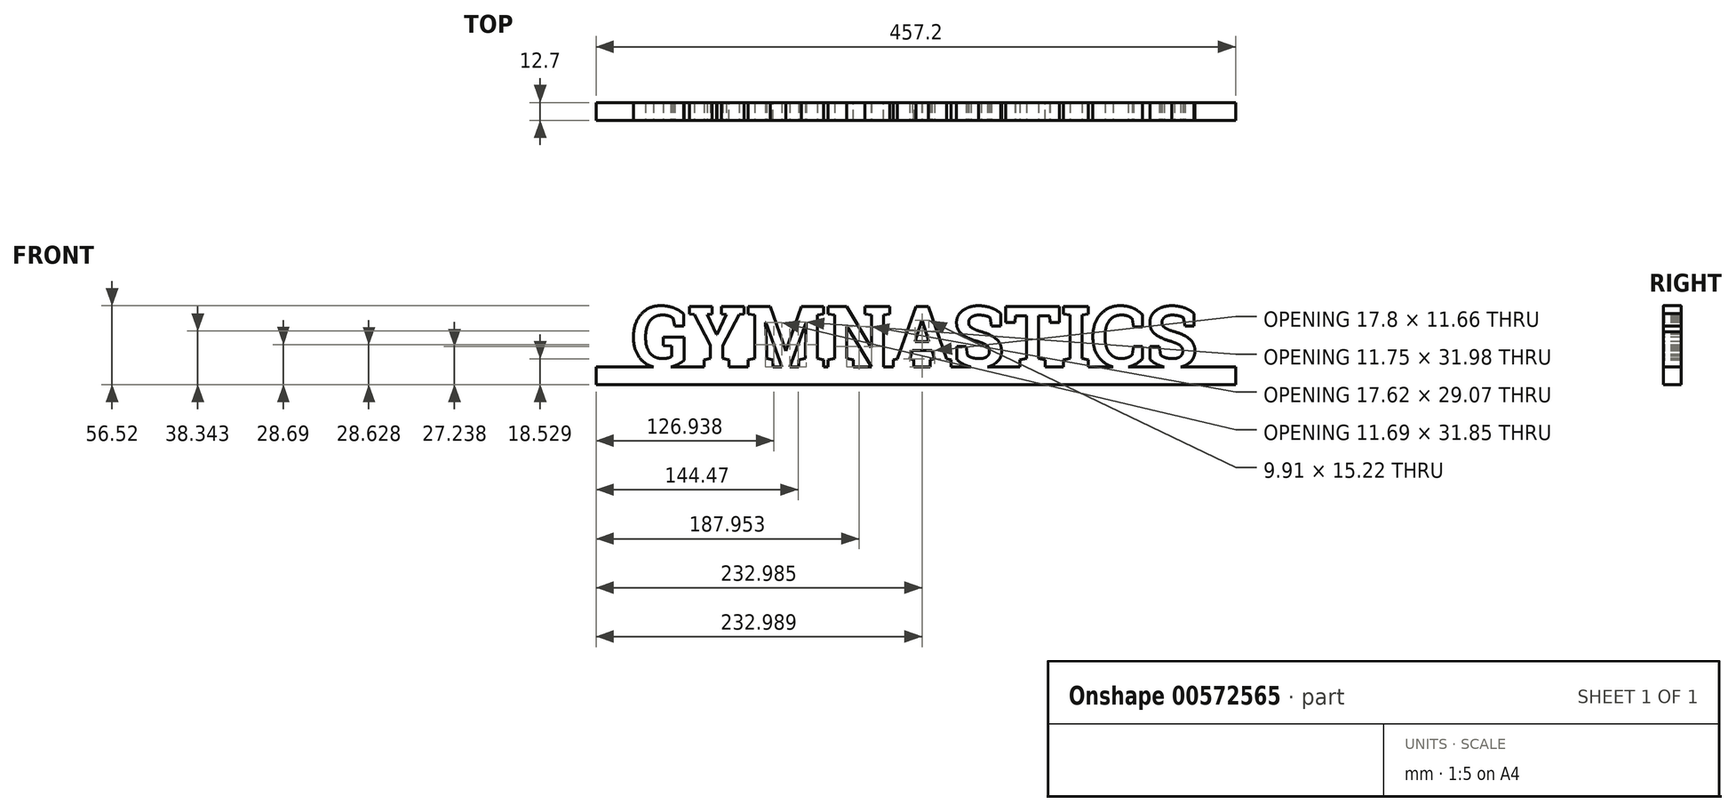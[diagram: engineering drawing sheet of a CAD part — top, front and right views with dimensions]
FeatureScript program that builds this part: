
annotation { "Feature Type Name" : "Feature", "Feature Type Description" : "" }
export const myFeature = defineFeature(function(context is Context, id is Id, definition is map)
    precondition{}
    {
        {
            var Q0;
            Q0=qCreatedBy(makeId("Front.planeOp"),FACE);
            var sketch = newSketch(context, id + "F0", { "sketchPlane" : qUnion([Q0])});
            skLineSegment(sketch, "E0.bottom", {"start": v(-211.92, -89.49) * mm, "end": v(245.28, -89.49) * mm});
            skLineSegment(sketch, "E0.top", {"start": v(-211.92, -102.19) * mm, "end": v(245.28, -102.19) * mm});
            skLineSegment(sketch, "E0.left", {"start": v(-211.92, -89.49) * mm, "end": v(-211.92, -102.19) * mm});
            skLineSegment(sketch, "E0.right", {"start": v(245.28, -89.49) * mm, "end": v(245.28, -102.19) * mm});
            skSolve(sketch);
        }
        {
            var Q0;
            Q0=makeQuery(id+"F0.imprint","IMPRINT",FACE,{"disambiguationData":[TD([[makeQuery(id+"F0.imprint","IMPRINT",EDGE,{"derivedFrom":sQuery(id+"F0.wireOp",EDGE,"E0.bottom")}),-1.0]])]});
            extrude(context, id + "F1", {"entities" : qUnion([Q0]), "depth" : 12.7 * mm, "offsetDistance" : 25.4 * mm});
        }
        {
            var Q0;
            Q0=makeQuery(id+"F1.opExtrude","CAP_FACE",FACE,{"disambiguationData":[OSD([sQuery(id+"F0.wireOp",EDGE,"E0.bottom"),sQuery(id+"F0.wireOp",EDGE,"E0.top"),sQuery(id+"F0.wireOp",EDGE,"E0.left"),sQuery(id+"F0.wireOp",EDGE,"E0.right")])],"isStart":false});
            var sketch = newSketch(context, id + "F2", { "sketchPlane" : qUnion([Q0])});
            skText(sketch, "E1", { "text": "GYMNASTICS", "fontName": "RobotoSlab-Bold.ttf"});
            skPoint(sketch, "E2", {"position": v(-186.52, -89.49) * mm});
            const initialGuessF2  = {"E1": [-0.18652, -0.08949, 1, 0, 0.04374]};
            skSetInitialGuess(sketch, initialGuessF2);
            skSolve(sketch);
        }
        {
            var Q0;
            Q0 = qSketchRegion(id + "F2", true);
            extrude(context, id + "F3", {"entities" : qUnion([Q0]), "operationType" : NewBodyOperationType.ADD, "depth" : -12.7 * mm, "offsetDistance" : 25.4 * mm});
        }
    });
